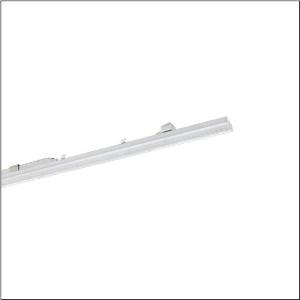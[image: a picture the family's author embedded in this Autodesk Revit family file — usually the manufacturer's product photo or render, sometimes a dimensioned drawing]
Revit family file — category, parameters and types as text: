
# Revit family: tl_l_5wd7a8f0g2c5
name_source: partatom
category: Lighting Fixtures
units: mm (PartAtom-declared; Revit-internal decimal feet)

## family parameters
Cut with Voids When Loaded = No
Host = Face
Light Source = No
Part Type = Normal
Room Calculation Point = No
Round Connector Dimension = Use Diameter
Shared = No

## types (1)
- TL L (1 x LED, 9800 lm, 63.3 W, 4000K)
    Apparent Load = 63 VA
    CIE Flux Codes = 49 84 98 100 100
    Color Rendering = 80
    Color Temperature = 4000K
    Default Elevation = 1800 mm
    Description = TL L, luminaire insert, of sheet steel, galvanised, coil coated, white, length: 1.500mm, width: 66mm, height: 67mm, surge protection,LED rated luminous flux: 9.800lm, light colour: 840, control gear: 4..20mA, with terminal, 5-pole, mains connection: 230..240V, AC, 50/60Hz, rated input power: 63W, primary optical cover: cover, of PMMA, light emission: direct distribution, protection rating (complete): as luminaire, insulation class (complete): insulation class I (protective earthing), certification: CE, impact resistance: IK06, permissible ambient temperature for indoor applications: -25..+35°C, packaging unit: 1 piece
    Height = 120 mm
    Lamp = 1 x LED
    Lamp Light Flux = 9800 lm
    Lamp Power = 63.3 W
    Lamp count = 1
    Length = 1690 mm
    Luminous efficacy = 155 lm/W
    Manufacturer = Siteco
    ModVariant = No
    Model = 5WD7A8F0G2C5
    Mounting Place = Ceiling
    Mounting Type = Pendant
    Number of Poles = 1
    OnlyDefault = Yes
    Power Factor = 1
    Product Name = TL L
    Product group = luminaire insert
    ProductGroupID = 901
    Protection Class = Protection class I
    Protection Degree = Degree of protection
    RLX_Detail_Level = 1
    RLX_Emergency_Light_Flux = 0 lm
    RLX_Emergency_Type = 0
    RLX_Emergency_Type_DB = No
    RlxData = <blob elided: 14145 chars, md5=722f52ff>
    Socket = socket
    Standby Power = 0 W
    System Light Flux = 9800 lm
    System Power = 63 W
    Type Comments = Product without accessories
    Type Image = l_1294382.jpg
    URL = http://relux.com
    VarID = ---
    Voltage = 0 V
    Weight = 0.00 kg
    Width = 208 mm

## geometry (parser evidence)
native form markers: Sweep x10
no freeform markers — native parametric forms only
